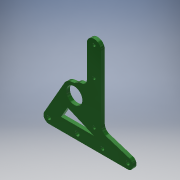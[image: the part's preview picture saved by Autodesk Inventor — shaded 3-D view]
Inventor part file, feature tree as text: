
AUTODESK INVENTOR PART (.ipt)
format: ipt  version: 2017 SP1 (Build 210196100, 196)  size: 166,400 bytes
history: native  units: in
note: dims shown in document units (in); Inventor stores cm internally (conversion verified against a paired STEP export)
features: reference x4, other x4, extrude x1, chamfer x1
ambient origin geometry x8: Origin, YZ Plane, XZ Plane, XY Plane, X Axis, Y Axis, Z Axis, Center Point
bodies: Solid1 (feature_tree)
feature tree (10):
  extrude  "Extrusion1"  Depth=0.21in
  chamfer  "Chamfer1"  Distance=3.0in
  reference  "Reference1"
  reference  "Reference2"
  reference  "Reference3"
  reference  "Reference4"
  other  "<userpath>\Desktop\Projects\2018 Robot\Cube Lift\Lift 3.iam"
  other  "Lift 3.iam"
  other  "2018_chassis:1"
  other  "am-2952a_AM14U3_Inside_Plate_4"
